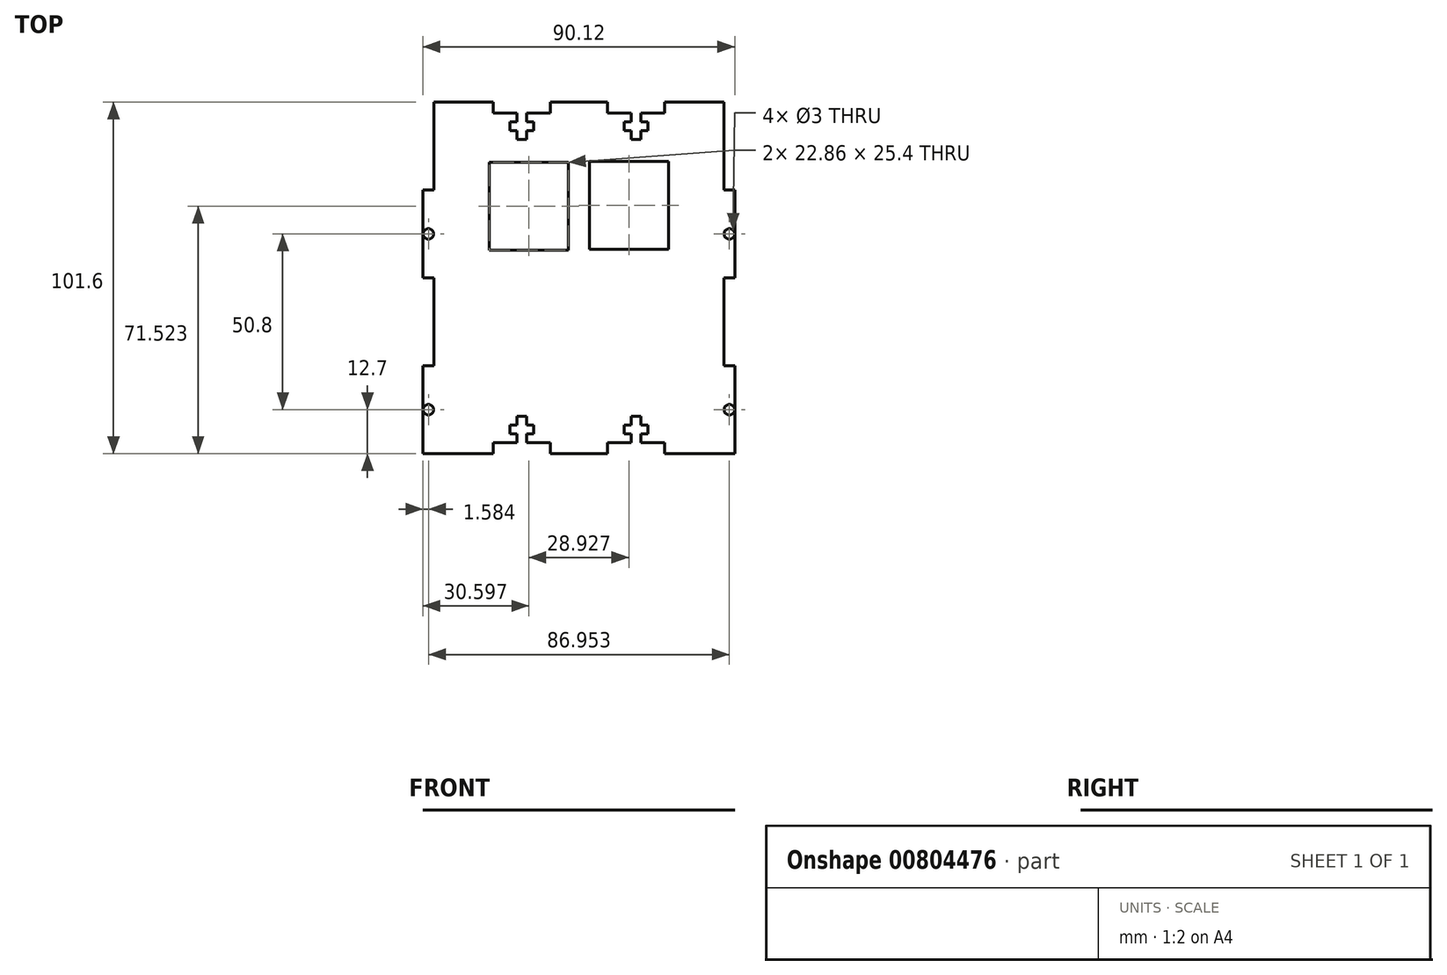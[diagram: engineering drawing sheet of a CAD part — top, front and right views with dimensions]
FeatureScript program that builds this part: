
annotation { "Feature Type Name" : "Feature", "Feature Type Description" : "" }
export const myFeature = defineFeature(function(context is Context, id is Id, definition is map)
    precondition{}
    {
        {
            var Q0;
            Q0=qCreatedBy(makeId("Top.planeOp"),FACE);
            var sketch = newSketch(context, id + "F0", { "sketchPlane" : qUnion([Q0])});
            skPoint(sketch, "E0.middle", {"position": v(0, 0) * mm});
            skLineSegment(sketch, "E1", {"start": v(-24.77, -63.5) * mm, "end": v(-24.77, -60.33) * mm});
            skLineSegment(sketch, "E2", {"start": v(-24.77, -60.33) * mm, "end": v(-17.9, -60.33) * mm});
            skLineSegment(sketch, "E3", {"start": v(-17.9, -60.33) * mm, "end": v(-17.9, -57.79) * mm});
            skLineSegment(sketch, "E4", {"start": v(-17.9, -57.79) * mm, "end": v(-19.94, -57.79) * mm});
            skLineSegment(sketch, "E5", {"start": v(-19.94, -57.79) * mm, "end": v(-19.94, -55.25) * mm});
            skLineSegment(sketch, "E6", {"start": v(-19.94, -55.25) * mm, "end": v(-17.9, -55.25) * mm});
            skLineSegment(sketch, "E7", {"start": v(-17.9, -55.25) * mm, "end": v(-17.9, -52.7) * mm});
            skLineSegment(sketch, "E8", {"start": v(-17.9, -52.7) * mm, "end": v(-15.11, -52.7) * mm});
            skLineSegment(sketch, "E9", {"start": v(-15.11, -52.7) * mm, "end": v(-15.11, -55.25) * mm});
            skLineSegment(sketch, "E10", {"start": v(-15.11, -55.25) * mm, "end": v(-13.08, -55.25) * mm});
            skLineSegment(sketch, "E11", {"start": v(-13.08, -55.25) * mm, "end": v(-13.08, -57.79) * mm});
            skLineSegment(sketch, "E12", {"start": v(-13.08, -57.79) * mm, "end": v(-15.11, -57.79) * mm});
            skLineSegment(sketch, "E13", {"start": v(-15.11, -57.79) * mm, "end": v(-15.11, -60.33) * mm});
            skLineSegment(sketch, "E14", {"start": v(-15.11, -60.33) * mm, "end": v(-8.26, -60.33) * mm});
            skLineSegment(sketch, "E15", {"start": v(-8.26, -60.33) * mm, "end": v(-8.26, -63.5) * mm});
            skLineSegment(sketch, "E16", {"start": v(-17.9, -55.25) * mm, "end": v(-15.11, -55.25) * mm, "construction": true});
            skLineSegment(sketch, "E17", {"start": v(-17.9, -57.79) * mm, "end": v(-15.11, -57.79) * mm, "construction": true});
            skLineSegment(sketch, "E18", {"start": v(-17.9, -60.33) * mm, "end": v(-15.11, -60.33) * mm, "construction": true});
            skLineSegment(sketch, "E19", {"start": v(-17.9, -55.25) * mm, "end": v(-17.9, -57.79) * mm, "construction": true});
            skLineSegment(sketch, "E20", {"start": v(-15.11, -55.25) * mm, "end": v(-15.11, -57.79) * mm, "construction": true});
            skLineSegment(sketch, "E21.MirrorCS", {"start": v(17.9, -55.25) * mm, "end": v(17.9, -57.79) * mm, "construction": true});
            skLineSegment(sketch, "E22.MirrorCS", {"start": v(15.11, -55.25) * mm, "end": v(15.11, -57.79) * mm, "construction": true});
            skLineSegment(sketch, "E23.MirrorCS", {"start": v(19.94, -57.79) * mm, "end": v(19.94, -55.25) * mm});
            skLineSegment(sketch, "E24.MirrorCS", {"start": v(13.08, -55.25) * mm, "end": v(13.08, -57.79) * mm});
            skLineSegment(sketch, "E25.MirrorCS", {"start": v(15.11, -57.79) * mm, "end": v(15.11, -60.33) * mm});
            skLineSegment(sketch, "E26.MirrorCS", {"start": v(8.25, -60.33) * mm, "end": v(8.25, -63.5) * mm});
            skLineSegment(sketch, "E27.MirrorCS", {"start": v(17.9, -57.79) * mm, "end": v(15.11, -57.79) * mm, "construction": true});
            skLineSegment(sketch, "E28.MirrorCS", {"start": v(17.9, -60.33) * mm, "end": v(17.9, -57.79) * mm});
            skLineSegment(sketch, "E29.MirrorCS", {"start": v(17.9, -57.79) * mm, "end": v(19.94, -57.79) * mm});
            skLineSegment(sketch, "E30.MirrorCS", {"start": v(24.77, -60.33) * mm, "end": v(17.9, -60.33) * mm});
            skLineSegment(sketch, "E31.MirrorCS", {"start": v(15.11, -52.7) * mm, "end": v(15.11, -55.25) * mm});
            skLineSegment(sketch, "E32.MirrorCS", {"start": v(17.9, -60.33) * mm, "end": v(15.11, -60.33) * mm, "construction": true});
            skLineSegment(sketch, "E33.MirrorCS", {"start": v(19.94, -55.25) * mm, "end": v(17.9, -55.25) * mm});
            skLineSegment(sketch, "E34.MirrorCS", {"start": v(24.76, -63.5) * mm, "end": v(24.76, -60.33) * mm});
            skLineSegment(sketch, "E35.MirrorCS", {"start": v(17.9, -55.25) * mm, "end": v(15.11, -55.25) * mm, "construction": true});
            skLineSegment(sketch, "E36.MirrorCS", {"start": v(17.9, -52.7) * mm, "end": v(15.11, -52.7) * mm});
            skLineSegment(sketch, "E37.MirrorCS", {"start": v(15.11, -55.25) * mm, "end": v(13.08, -55.25) * mm});
            skLineSegment(sketch, "E38.MirrorCS", {"start": v(15.11, -60.33) * mm, "end": v(8.26, -60.33) * mm});
            skLineSegment(sketch, "E39.MirrorCS", {"start": v(13.08, -57.79) * mm, "end": v(15.11, -57.79) * mm});
            skLineSegment(sketch, "E40.MirrorCS", {"start": v(17.9, -55.25) * mm, "end": v(17.9, -52.7) * mm});
            skLineSegment(sketch, "E41", {"start": v(-41.89, 38.1) * mm, "end": v(-24.76, 38.1) * mm});
            skLineSegment(sketch, "E42", {"start": v(24.76, 38.1) * mm, "end": v(41.89, 38.1) * mm});
            skLineSegment(sketch, "E43", {"start": v(-41.91, -63.5) * mm, "end": v(-24.77, -63.5) * mm});
            skLineSegment(sketch, "E44", {"start": v(-8.26, -63.5) * mm, "end": v(8.26, -63.5) * mm});
            skLineSegment(sketch, "E45", {"start": v(24.77, -63.5) * mm, "end": v(41.91, -63.5) * mm});
            skLineSegment(sketch, "E46", {"start": v(-41.91, -12.7) * mm, "end": v(41.91, -12.7) * mm, "construction": true});
            skLineSegment(sketch, "E47.MirrorCS", {"start": v(13.08, 32.39) * mm, "end": v(15.11, 32.39) * mm});
            skLineSegment(sketch, "E48.MirrorCS", {"start": v(13.08, 29.85) * mm, "end": v(13.08, 32.39) * mm});
            skLineSegment(sketch, "E49.MirrorCS", {"start": v(17.9, 29.85) * mm, "end": v(17.9, 32.39) * mm, "construction": true});
            skLineSegment(sketch, "E50.MirrorCS", {"start": v(15.11, 32.39) * mm, "end": v(15.11, 34.93) * mm});
            skLineSegment(sketch, "E51.MirrorCS", {"start": v(17.9, 34.93) * mm, "end": v(17.9, 32.39) * mm});
            skLineSegment(sketch, "E52.MirrorCS", {"start": v(17.9, 32.39) * mm, "end": v(15.11, 32.39) * mm, "construction": true});
            skLineSegment(sketch, "E53.MirrorCS", {"start": v(15.11, 29.85) * mm, "end": v(15.11, 32.39) * mm, "construction": true});
            skLineSegment(sketch, "E54.MirrorCS", {"start": v(-17.9, 29.85) * mm, "end": v(-17.9, 27.3) * mm});
            skLineSegment(sketch, "E55.MirrorCS", {"start": v(-17.9, 29.85) * mm, "end": v(-17.9, 32.39) * mm, "construction": true});
            skLineSegment(sketch, "E56.MirrorCS", {"start": v(19.94, 32.39) * mm, "end": v(19.94, 29.85) * mm});
            skLineSegment(sketch, "E57.MirrorCS", {"start": v(-19.94, 29.85) * mm, "end": v(-17.9, 29.85) * mm});
            skLineSegment(sketch, "E58.MirrorCS", {"start": v(17.9, 32.39) * mm, "end": v(19.94, 32.39) * mm});
            skLineSegment(sketch, "E59.MirrorCS", {"start": v(-15.11, 29.85) * mm, "end": v(-13.08, 29.85) * mm});
            skLineSegment(sketch, "E60.MirrorCS", {"start": v(-13.08, 29.85) * mm, "end": v(-13.08, 32.39) * mm});
            skLineSegment(sketch, "E61.MirrorCS", {"start": v(-15.11, 27.3) * mm, "end": v(-15.11, 29.85) * mm});
            skLineSegment(sketch, "E62.MirrorCS", {"start": v(-19.94, 32.39) * mm, "end": v(-19.94, 29.85) * mm});
            skLineSegment(sketch, "E63.MirrorCS", {"start": v(-15.11, 29.85) * mm, "end": v(-15.11, 32.39) * mm, "construction": true});
            skLineSegment(sketch, "E64.MirrorCS", {"start": v(-17.9, 29.85) * mm, "end": v(-15.11, 29.85) * mm, "construction": true});
            skLineSegment(sketch, "E65.MirrorCS", {"start": v(19.94, 29.85) * mm, "end": v(17.9, 29.85) * mm});
            skLineSegment(sketch, "E66.MirrorCS", {"start": v(15.11, 29.85) * mm, "end": v(13.08, 29.85) * mm});
            skLineSegment(sketch, "E67.MirrorCS", {"start": v(17.9, 29.85) * mm, "end": v(17.9, 27.3) * mm});
            skLineSegment(sketch, "E68.MirrorCS", {"start": v(-13.08, 32.39) * mm, "end": v(-15.11, 32.39) * mm});
            skLineSegment(sketch, "E69.MirrorCS", {"start": v(-15.11, 32.39) * mm, "end": v(-15.11, 34.93) * mm});
            skLineSegment(sketch, "E70.MirrorCS", {"start": v(-17.9, 34.93) * mm, "end": v(-17.9, 32.39) * mm});
            skLineSegment(sketch, "E71.MirrorCS", {"start": v(15.11, 27.3) * mm, "end": v(15.11, 29.85) * mm});
            skLineSegment(sketch, "E72.MirrorCS", {"start": v(17.9, 29.85) * mm, "end": v(15.11, 29.85) * mm, "construction": true});
            skLineSegment(sketch, "E73.MirrorCS", {"start": v(-17.9, 32.39) * mm, "end": v(-15.11, 32.39) * mm, "construction": true});
            skLineSegment(sketch, "E74.MirrorCS", {"start": v(-17.9, 32.39) * mm, "end": v(-19.94, 32.39) * mm});
            skLineSegment(sketch, "E75.MirrorCS", {"start": v(-17.9, 27.3) * mm, "end": v(-15.11, 27.3) * mm});
            skLineSegment(sketch, "E76.MirrorCS", {"start": v(17.9, 34.93) * mm, "end": v(15.11, 34.93) * mm, "construction": true});
            skLineSegment(sketch, "E77.MirrorCS", {"start": v(-17.9, 34.93) * mm, "end": v(-15.11, 34.93) * mm, "construction": true});
            skLineSegment(sketch, "E78.MirrorCS", {"start": v(17.9, 27.3) * mm, "end": v(15.11, 27.3) * mm});
            skLineSegment(sketch, "E79.MirrorCS", {"start": v(8.25, 34.93) * mm, "end": v(8.25, 38.1) * mm});
            skLineSegment(sketch, "E80.MirrorCS", {"start": v(24.76, 38.1) * mm, "end": v(24.76, 34.93) * mm});
            skLineSegment(sketch, "E81.MirrorCS", {"start": v(-8.25, 34.93) * mm, "end": v(-8.25, 38.1) * mm});
            skLineSegment(sketch, "E82.MirrorCS", {"start": v(-24.76, 38.1) * mm, "end": v(-24.76, 34.93) * mm});
            skLineSegment(sketch, "E83.MirrorCS", {"start": v(-15.11, 34.93) * mm, "end": v(-8.25, 34.93) * mm});
            skLineSegment(sketch, "E84.MirrorCS", {"start": v(-24.76, 34.93) * mm, "end": v(-17.9, 34.93) * mm});
            skLineSegment(sketch, "E85.MirrorCS", {"start": v(15.11, 34.93) * mm, "end": v(8.26, 34.93) * mm});
            skLineSegment(sketch, "E86.MirrorCS", {"start": v(24.77, 34.93) * mm, "end": v(17.9, 34.93) * mm});
            skLineSegment(sketch, "E87.MirrorCS", {"start": v(-8.25, 38.1) * mm, "end": v(8.26, 38.1) * mm});
            skLineSegment(sketch, "E88", {"start": v(41.89, 12.7) * mm, "end": v(45.06, 12.7) * mm});
            skLineSegment(sketch, "E89", {"start": v(45.06, 12.7) * mm, "end": v(45.06, -12.7) * mm});
            skLineSegment(sketch, "E90", {"start": v(41.89, -12.7) * mm, "end": v(45.06, -12.7) * mm});
            skLineSegment(sketch, "E91", {"start": v(41.89, 38.1) * mm, "end": v(41.89, 12.7) * mm});
            skLineSegment(sketch, "E92.1.0.0", {"start": v(45.06, -38.1) * mm, "end": v(45.06, -63.5) * mm});
            skLineSegment(sketch, "E92.1.0.1", {"start": v(41.89, -38.1) * mm, "end": v(45.06, -38.1) * mm});
            skLineSegment(sketch, "E92.1.0.2", {"start": v(41.89, -12.7) * mm, "end": v(41.89, -38.1) * mm});
            skLineSegment(sketch, "E92.1.0.3", {"start": v(41.89, -63.5) * mm, "end": v(45.06, -63.5) * mm});
            skLineSegment(sketch, "E92.direction1", {"start": v(41.89, -12.7) * mm, "end": v(41.89, -63.5) * mm, "construction": true});
            skLineSegment(sketch, "E93.MirrorCS", {"start": v(-41.89, -63.5) * mm, "end": v(-45.06, -63.5) * mm});
            skLineSegment(sketch, "E94.MirrorCS", {"start": v(-45.06, -38.1) * mm, "end": v(-45.06, -63.5) * mm});
            skLineSegment(sketch, "E95.MirrorCS", {"start": v(-41.89, -38.1) * mm, "end": v(-45.06, -38.1) * mm});
            skLineSegment(sketch, "E96.MirrorCS", {"start": v(-41.89, 12.7) * mm, "end": v(-45.06, 12.7) * mm});
            skLineSegment(sketch, "E97.MirrorCS", {"start": v(-41.89, -12.7) * mm, "end": v(-45.06, -12.7) * mm});
            skLineSegment(sketch, "E98.MirrorCS", {"start": v(-45.06, 12.7) * mm, "end": v(-45.06, -12.7) * mm});
            skLineSegment(sketch, "E99.MirrorCS", {"start": v(-41.89, -12.7) * mm, "end": v(-41.89, -63.5) * mm, "construction": true});
            skLineSegment(sketch, "E100.MirrorCS", {"start": v(41.91, -12.7) * mm, "end": v(-41.91, -12.7) * mm, "construction": true});
            skLineSegment(sketch, "E101.MirrorCS", {"start": v(-24.77, -63.5) * mm, "end": v(-41.91, -63.5) * mm});
            skLineSegment(sketch, "E102.MirrorCS", {"start": v(-41.89, -12.7) * mm, "end": v(-41.89, -38.1) * mm});
            skLineSegment(sketch, "E103.MirrorCS", {"start": v(-41.89, 38.1) * mm, "end": v(-41.89, 12.7) * mm});
            skCircle(sketch, "E104", {"center": v(-43.48, 0) * mm, "radius": 1.5 * mm});
            skLineSegment(sketch, "E105", {"start": v(-43.48, 12.7) * mm, "end": v(-43.48, 0) * mm, "construction": true});
            skLineSegment(sketch, "E106", {"start": v(-43.48, 0) * mm, "end": v(-43.48, -12.7) * mm, "construction": true});
            skLineSegment(sketch, "E107", {"start": v(-43.48, 0) * mm, "end": v(-43.48, -50.8) * mm, "construction": true});
            skCircle(sketch, "E108", {"center": v(-43.48, -50.8) * mm, "radius": 1.5 * mm});
            skCircle(sketch, "E109.MirrorC", {"center": v(43.48, 0) * mm, "radius": 1.5 * mm});
            skCircle(sketch, "E110.MirrorC", {"center": v(43.48, -50.8) * mm, "radius": 1.5 * mm});
            skLineSegment(sketch, "E111", {"start": v(0, 38.1) * mm, "end": v(0, 19.85) * mm, "construction": true});
            skLineSegment(sketch, "E112.bottom", {"start": v(-25.9, 20.72) * mm, "end": v(-3.03, 20.72) * mm});
            skLineSegment(sketch, "E112.top", {"start": v(-25.9, -4.68) * mm, "end": v(-3.03, -4.68) * mm});
            skLineSegment(sketch, "E112.left", {"start": v(-25.9, 20.72) * mm, "end": v(-25.9, -4.68) * mm});
            skLineSegment(sketch, "E112.right", {"start": v(-3.03, 20.72) * mm, "end": v(-3.03, -4.68) * mm});
            skLineSegment(sketch, "E113.bottom", {"start": v(25.9, 20.98) * mm, "end": v(3.03, 20.98) * mm});
            skLineSegment(sketch, "E113.top", {"start": v(25.9, -4.42) * mm, "end": v(3.03, -4.42) * mm});
            skLineSegment(sketch, "E113.left", {"start": v(25.9, 20.98) * mm, "end": v(25.9, -4.42) * mm});
            skLineSegment(sketch, "E113.right", {"start": v(3.03, 20.98) * mm, "end": v(3.03, -4.42) * mm});
            skLineSegment(sketch, "E114", {"start": v(0, 19.85) * mm, "end": v(-3.03, 19.85) * mm, "construction": true});
            skLineSegment(sketch, "E115", {"start": v(0, 19.85) * mm, "end": v(3.03, 19.85) * mm, "construction": true});
            skSolve(sketch);
        }
        {
            var Q0;
            Q0=makeQuery(id+"F0.imprint","IMPRINT",FACE,{"disambiguationData":[TD([[makeQuery(id+"F0.imprint","IMPRINT",EDGE,{"derivedFrom":sQuery(id+"F0.wireOp",EDGE,"E1")}),1.0]])]});
            extrude(context, id + "F1", {"entities" : qUnion([Q0]), "depth" : 1 / 203.2 * mm, "offsetDistance" : 25.4 * mm});
        }
    });
